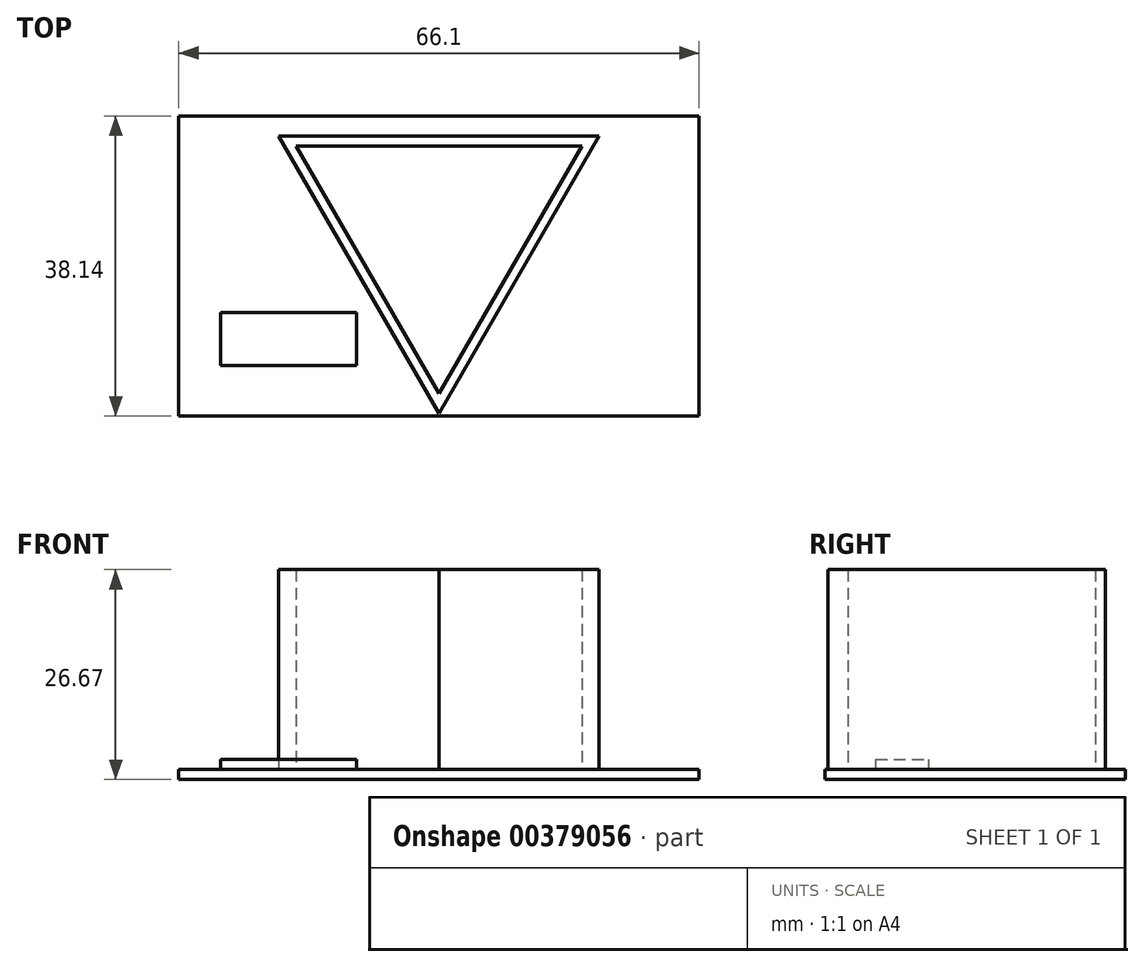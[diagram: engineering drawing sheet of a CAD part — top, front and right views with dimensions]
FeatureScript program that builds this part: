
annotation { "Feature Type Name" : "Feature", "Feature Type Description" : "" }
export const myFeature = defineFeature(function(context is Context, id is Id, definition is map)
    precondition{}
    {
        {
            var Q0;
            Q0=qCreatedBy(makeId("Top.planeOp"),FACE);
            var sketch = newSketch(context, id + "F0", { "sketchPlane" : qUnion([Q0])});
            skLineSegment(sketch, "E0.bottom", {"start": v(33.05, 19.07) * mm, "end": v(-33.05, 19.07) * mm});
            skLineSegment(sketch, "E0.top", {"start": v(33.05, -19.07) * mm, "end": v(-33.05, -19.07) * mm});
            skLineSegment(sketch, "E0.left", {"start": v(33.05, 19.07) * mm, "end": v(33.05, -19.07) * mm});
            skLineSegment(sketch, "E0.right", {"start": v(-33.05, 19.07) * mm, "end": v(-33.05, -19.07) * mm});
            skPoint(sketch, "E0.middle", {"position": v(0, 0) * mm});
            skSolve(sketch);
        }
        {
            var Q0;
            Q0=makeQuery(id+"F0.imprint","IMPRINT",FACE,{"disambiguationData":[TD([[makeQuery(id+"F0.imprint","IMPRINT",EDGE,{"derivedFrom":sQuery(id+"F0.wireOp",EDGE,"E0.bottom")}),1.0]])]});
            extrude(context, id + "F1", {"entities" : qUnion([Q0]), "depth" : 1.27 * mm});
        }
        {
            var Q0;
            Q0=makeQuery(id+"F1.opExtrude","CAP_FACE",FACE,{"disambiguationData":[OSD([sQuery(id+"F0.wireOp",EDGE,"E0.bottom"),sQuery(id+"F0.wireOp",EDGE,"E0.top"),sQuery(id+"F0.wireOp",EDGE,"E0.left"),sQuery(id+"F0.wireOp",EDGE,"E0.right")])],"isStart":false});
            var sketch = newSketch(context, id + "F2", { "sketchPlane" : qUnion([Q0])});
            skLineSegment(sketch, "E1", {"start": v(-20.35, 16.53) * mm, "end": v(20.35, 16.53) * mm});
            skLineSegment(sketch, "E2", {"start": v(20.35, 16.53) * mm, "end": v(0, -18.72) * mm});
            skLineSegment(sketch, "E3", {"start": v(0, -18.72) * mm, "end": v(-20.35, 16.53) * mm});
            skSolve(sketch);
        }
        {
            var Q0;
            Q0 = qSketchRegion(id + "F2", true);
            extrude(context, id + "F3", {"entities" : qUnion([Q0]), "operationType" : NewBodyOperationType.ADD, "depth" : 25.4 * mm});
        }
        {
            var Q0;
            Q0=makeQuery(id+"F3.opExtrude","CAP_FACE",FACE,{"disambiguationData":[OSD([sQuery(id+"F2.wireOp",EDGE,"E1"),sQuery(id+"F2.wireOp",EDGE,"E2"),sQuery(id+"F2.wireOp",EDGE,"E3")])],"isStart":false});
            shell(context, id + "F4", {"entities" : qUnion([Q0]), "thickness" : 1.27 * mm});
        }
        {
            var Q0;
            Q0=makeQuery(id+"F1.opExtrude","CAP_FACE",FACE,{"disambiguationData":[OSD([sQuery(id+"F0.wireOp",EDGE,"E0.bottom"),sQuery(id+"F0.wireOp",EDGE,"E0.top"),sQuery(id+"F0.wireOp",EDGE,"E0.left"),sQuery(id+"F0.wireOp",EDGE,"E0.right")])],"isStart":false});
            var sketch = newSketch(context, id + "F5", { "sketchPlane" : qUnion([Q0])});
            skLineSegment(sketch, "E4.bottom", {"start": v(-27.74, -12.65) * mm, "end": v(-10.45, -12.65) * mm});
            skLineSegment(sketch, "E4.top", {"start": v(-27.74, -5.93) * mm, "end": v(-10.45, -5.93) * mm});
            skLineSegment(sketch, "E4.left", {"start": v(-27.74, -12.65) * mm, "end": v(-27.74, -5.93) * mm});
            skLineSegment(sketch, "E4.right", {"start": v(-10.45, -12.65) * mm, "end": v(-10.45, -5.93) * mm});
            skSolve(sketch);
        }
        {
            var Q0;
            Q0 = qSketchRegion(id + "F5", true);
            extrude(context, id + "F6", {"entities" : qUnion([Q0]), "operationType" : NewBodyOperationType.ADD, "depth" : 1.27 * mm});
        }
    });
